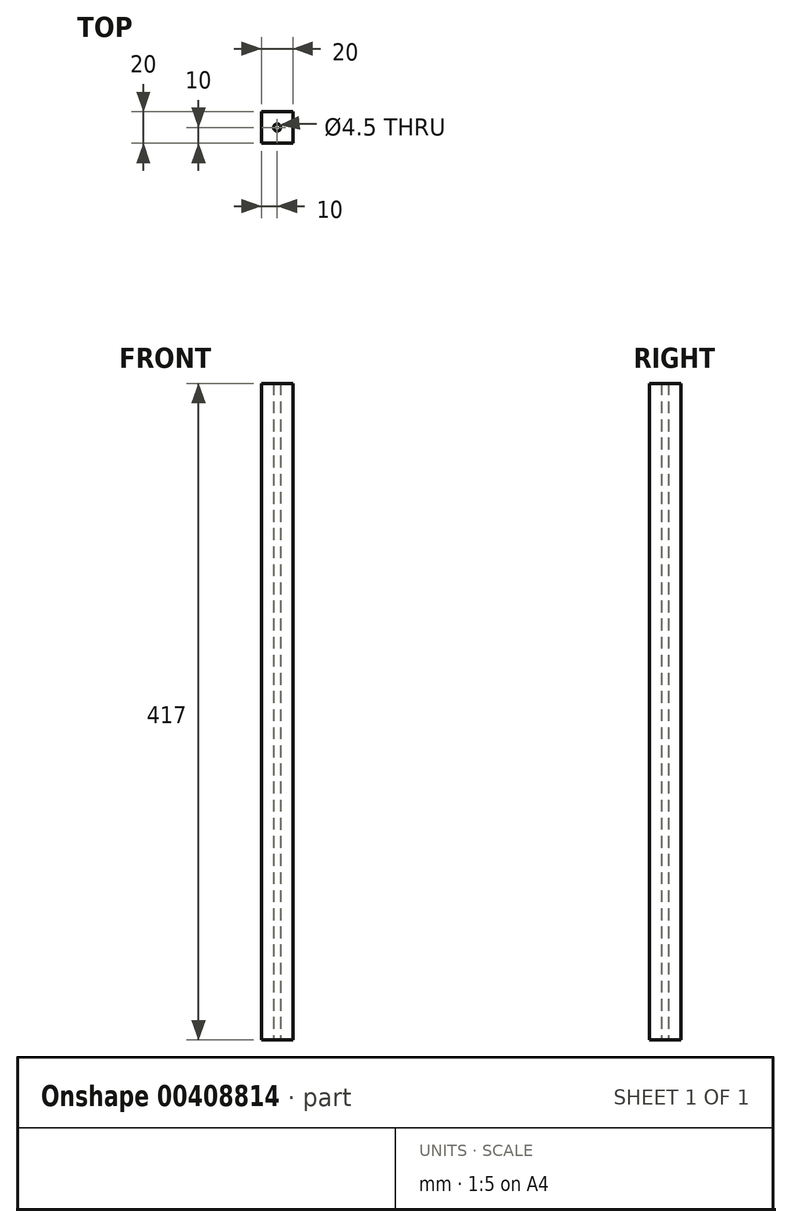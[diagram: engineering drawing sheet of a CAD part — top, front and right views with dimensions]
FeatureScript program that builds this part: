
annotation { "Feature Type Name" : "Feature", "Feature Type Description" : "" }
export const myFeature = defineFeature(function(context is Context, id is Id, definition is map)
    precondition{}
    {
        {
            var Q0;
            Q0=qCreatedBy(makeId("Top.planeOp"),FACE);
            var sketch = newSketch(context, id + "F0", { "sketchPlane" : qUnion([Q0])});
            skLineSegment(sketch, "E0.bottom", {"start": v(10, -10) * mm, "end": v(-10, -10) * mm});
            skLineSegment(sketch, "E0.top", {"start": v(10, 10) * mm, "end": v(-10, 10) * mm});
            skLineSegment(sketch, "E0.left", {"start": v(10, -10) * mm, "end": v(10, 10) * mm});
            skLineSegment(sketch, "E0.right", {"start": v(-10, -10) * mm, "end": v(-10, 10) * mm});
            skPoint(sketch, "E0.middle", {"position": v(0, 0) * mm});
            skCircle(sketch, "E1", {"center": v(0, 0) * mm, "radius": 2.25 * mm});
            skSolve(sketch);
        }
        {
            var Q0;
            Q0=makeQuery(id+"F0.imprint","IMPRINT",FACE,{"disambiguationData":[TD([[makeQuery(id+"F0.imprint","IMPRINT",EDGE,{"derivedFrom":sQuery(id+"F0.wireOp",EDGE,"E0.bottom")}),-1.0]])]});
            extrude(context, id + "F1", {"entities" : qUnion([Q0]), "depth" : 417 * mm});
        }
    });
